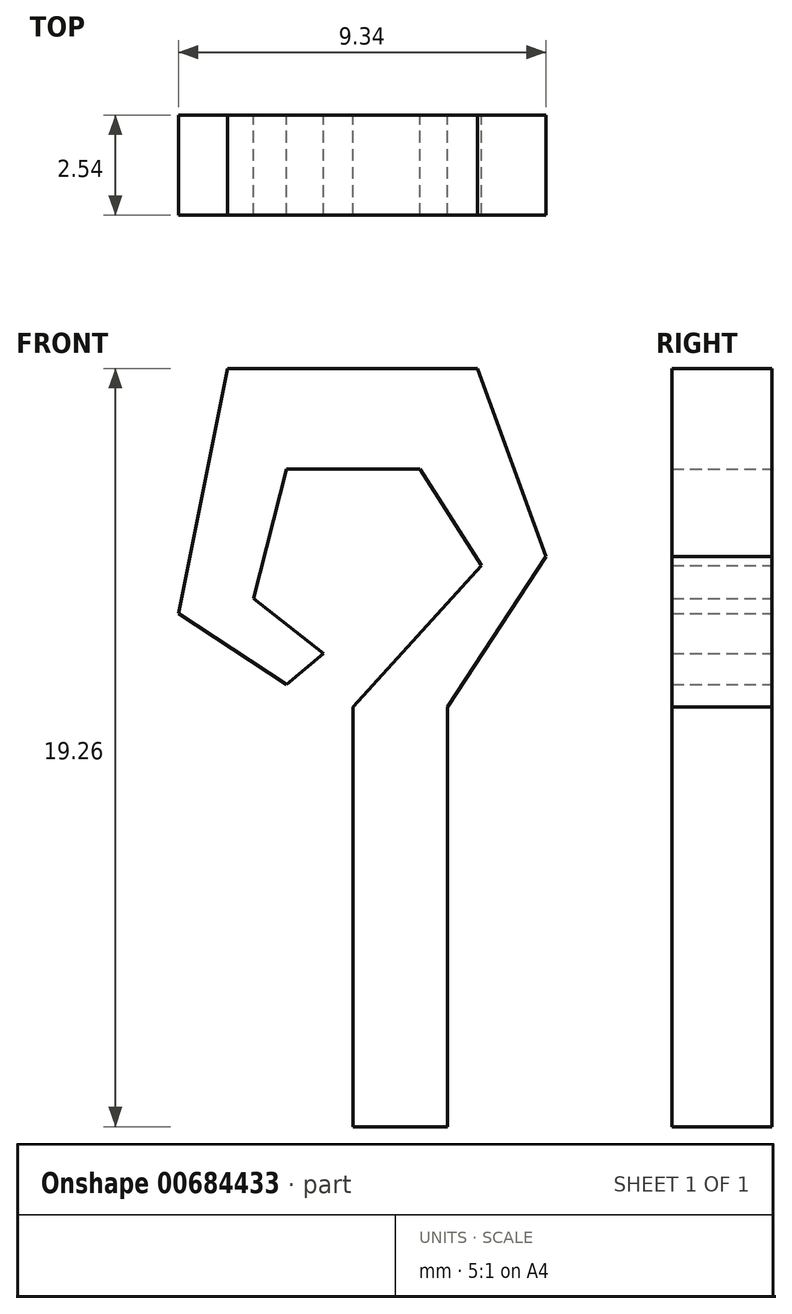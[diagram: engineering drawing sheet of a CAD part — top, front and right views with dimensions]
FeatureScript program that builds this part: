
annotation { "Feature Type Name" : "Feature", "Feature Type Description" : "" }
export const myFeature = defineFeature(function(context is Context, id is Id, definition is map)
    precondition{}
    {
        {
            var Q0;
            Q0=qCreatedBy(makeId("Front.planeOp"),FACE);
            var sketch = newSketch(context, id + "F0", { "sketchPlane" : qUnion([Q0])});
            skLineSegment(sketch, "E0", {"start": v(17.64, 46.6) * mm, "end": v(17.64, 35.94) * mm});
            skLineSegment(sketch, "E1", {"start": v(17.64, 35.94) * mm, "end": v(20.03, 35.94) * mm});
            skLineSegment(sketch, "E2", {"start": v(20.03, 35.94) * mm, "end": v(20.03, 46.6) * mm});
            skLineSegment(sketch, "E3", {"start": v(20.03, 46.6) * mm, "end": v(22.54, 50.43) * mm});
            skLineSegment(sketch, "E4", {"start": v(22.54, 50.43) * mm, "end": v(20.8, 55.2) * mm});
            skLineSegment(sketch, "E5", {"start": v(20.8, 55.2) * mm, "end": v(14.45, 55.2) * mm});
            skLineSegment(sketch, "E6", {"start": v(14.45, 55.2) * mm, "end": v(13.2, 48.98) * mm});
            skLineSegment(sketch, "E7", {"start": v(13.2, 48.98) * mm, "end": v(15.95, 47.17) * mm});
            skLineSegment(sketch, "E8", {"start": v(17.64, 46.6) * mm, "end": v(20.9, 50.2) * mm});
            skLineSegment(sketch, "E9", {"start": v(20.9, 50.2) * mm, "end": v(19.34, 52.65) * mm});
            skLineSegment(sketch, "E10", {"start": v(19.34, 52.65) * mm, "end": v(15.95, 52.65) * mm});
            skLineSegment(sketch, "E11", {"start": v(15.95, 52.65) * mm, "end": v(15.1, 49.36) * mm});
            skLineSegment(sketch, "E12", {"start": v(15.1, 49.36) * mm, "end": v(16.9, 47.96) * mm});
            skLineSegment(sketch, "E13", {"start": v(16.9, 47.96) * mm, "end": v(15.95, 47.17) * mm});
            skSolve(sketch);
        }
        {
            var Q0;
            Q0 = qSketchRegion(id + "F0", true);
            extrude(context, id + "F1", {"entities" : qUnion([Q0]), "depth" : 2.54 * mm, "offsetDistance" : 25.4 * mm});
        }
    });
